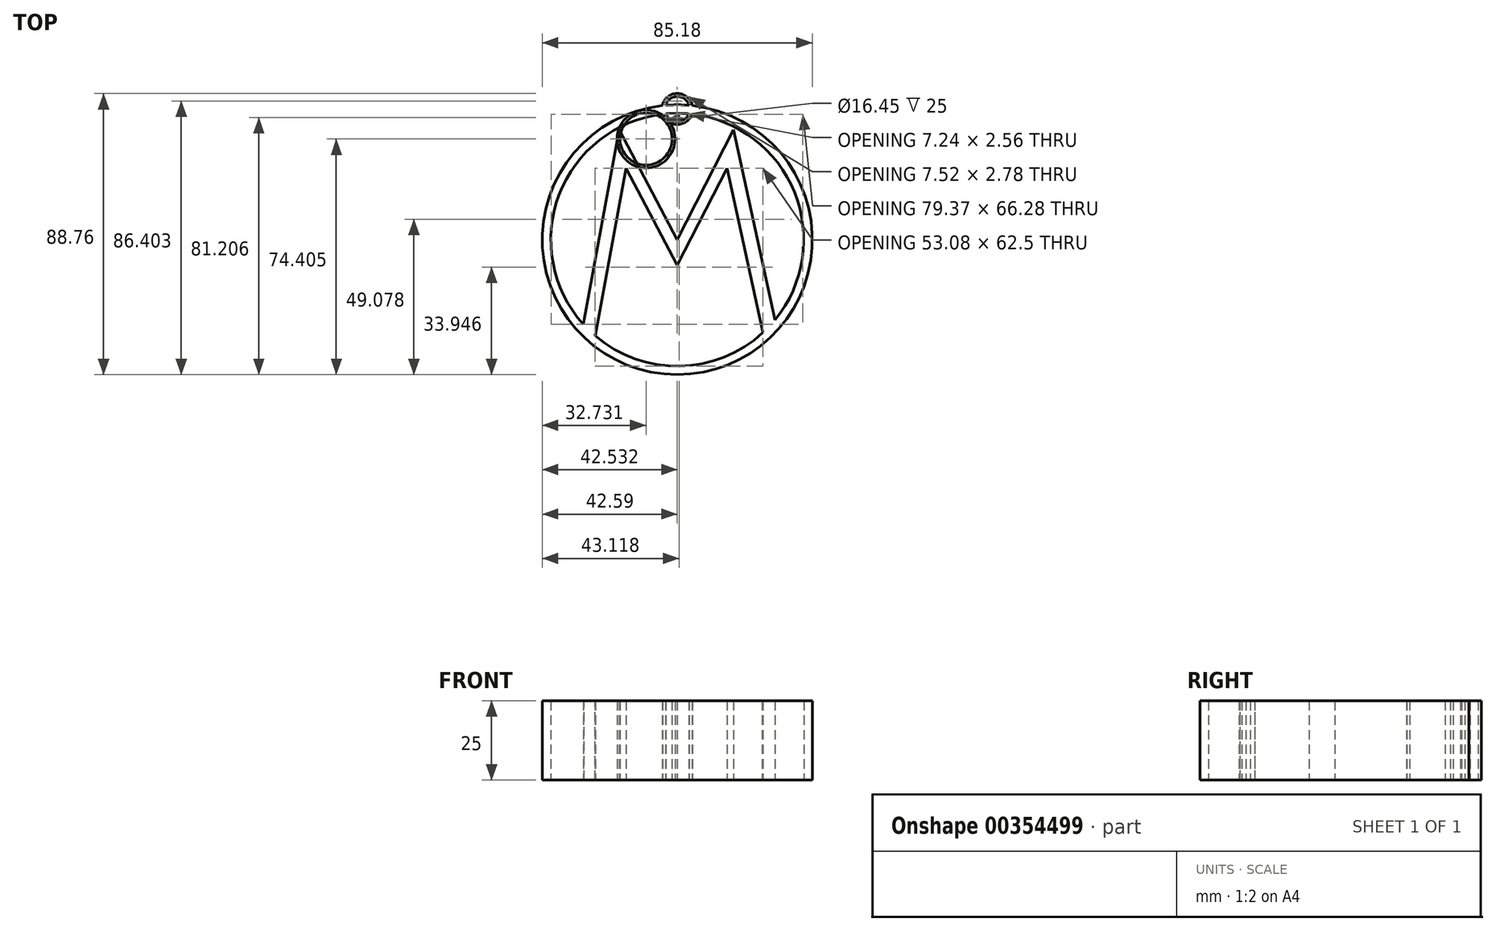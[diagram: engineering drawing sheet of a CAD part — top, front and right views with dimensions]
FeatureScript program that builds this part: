
annotation { "Feature Type Name" : "Feature", "Feature Type Description" : "" }
export const myFeature = defineFeature(function(context is Context, id is Id, definition is map)
    precondition{}
    {
        {
            var Q0;
            Q0=qCreatedBy(makeId("Top.planeOp"),FACE);
            var sketch = newSketch(context, id + "F0", { "sketchPlane" : qUnion([Q0])});
            skCircle(sketch, "E0", {"center": v(0, 0) * mm, "radius": 42.6 * mm});
            skCircle(sketch, "E1", {"center": v(0, 0) * mm, "radius": 39.9 * mm});
            skSolve(sketch);
        }
        {
            var Q0;
            Q0 = qSketchRegion(id + "F0", true);
            extrude(context, id + "F1", {"entities" : qUnion([Q0]), "depth" : 25 * mm});
        }
        {
            var Q0;
            Q0=qCreatedBy(makeId("Top.planeOp"),FACE);
            var sketch = newSketch(context, id + "F2", { "sketchPlane" : qUnion([Q0])});
            skLineSegment(sketch, "E2", {"start": v(-29.44, -25.55) * mm, "end": v(-18.38, 34.82) * mm});
            skLineSegment(sketch, "E3", {"start": v(-18.38, 34.82) * mm, "end": v(0, 0) * mm});
            skLineSegment(sketch, "E4", {"start": v(0, 0) * mm, "end": v(17.78, 34.82) * mm});
            skLineSegment(sketch, "E5", {"start": v(17.78, 34.82) * mm, "end": v(30.93, -25.55) * mm});
            skLineSegment(sketch, "E6", {"start": v(-25.85, -30.04) * mm, "end": v(-16.2, 22.6) * mm});
            skLineSegment(sketch, "E7", {"start": v(-16.2, 22.6) * mm, "end": v(0, -8.1) * mm});
            skLineSegment(sketch, "E8", {"start": v(0, -8.1) * mm, "end": v(15.68, 22.6) * mm});
            skLineSegment(sketch, "E9", {"start": v(15.68, 22.6) * mm, "end": v(26.72, -28.08) * mm});
            skLineSegment(sketch, "E10", {"start": v(-29.44, -25.55) * mm, "end": v(-25.85, -30.04) * mm});
            skLineSegment(sketch, "E11", {"start": v(26.72, -28.08) * mm, "end": v(30.93, -25.55) * mm});
            skLineSegment(sketch, "E12", {"start": v(30.93, -25.55) * mm, "end": v(26.72, -30.04) * mm});
            skLineSegment(sketch, "E13", {"start": v(26.72, -30.04) * mm, "end": v(30.93, -25.55) * mm});
            skLineSegment(sketch, "E14", {"start": v(-25.85, -30.04) * mm, "end": v(-29.44, -29.38) * mm});
            skLineSegment(sketch, "E15", {"start": v(-29.44, -25.55) * mm, "end": v(-29.44, -29.38) * mm});
            skSolve(sketch);
        }
        {
            var Q0;
            Q0=makeQuery(id+"F2.imprint","IMPRINT",FACE,{"disambiguationData":[TD([[makeQuery(id+"F2.imprint","IMPRINT",EDGE,{"derivedFrom":sQuery(id+"F2.wireOp",EDGE,"E2")}),-1.0]])]});
            extrude(context, id + "F3", {"entities" : qUnion([Q0]), "operationType" : NewBodyOperationType.ADD, "depth" : 25 * mm});
        }
        {
            var Q0;
            Q0=qCreatedBy(makeId("Top.planeOp"),FACE);
            var sketch = newSketch(context, id + "F4", { "sketchPlane" : qUnion([Q0])});
            skLineSegment(sketch, "E16", {"start": v(-29.13, -24.09) * mm, "end": v(-30.02, -28.17) * mm});
            skLineSegment(sketch, "E17", {"start": v(-30.02, -28.17) * mm, "end": v(-26.38, -32) * mm});
            skLineSegment(sketch, "E18", {"start": v(-26.38, -32) * mm, "end": v(-25.58, -28.17) * mm});
            skLineSegment(sketch, "E19", {"start": v(-25.58, -28.17) * mm, "end": v(-29.13, -24.09) * mm});
            skSolve(sketch);
        }
        {
            var Q0;
            Q0 = qSketchRegion(id + "F4", true);
            extrude(context, id + "F5", {"entities" : qUnion([Q0]), "operationType" : NewBodyOperationType.ADD, "depth" : 25 * mm});
        }
        {
            var Q0;
            Q0=qCreatedBy(makeId("Top.planeOp"),FACE);
            var sketch = newSketch(context, id + "F6", { "sketchPlane" : qUnion([Q0])});
            skLineSegment(sketch, "E20", {"start": v(26.4, -26.49) * mm, "end": v(27.47, -31.02) * mm});
            skLineSegment(sketch, "E21", {"start": v(27.47, -31.02) * mm, "end": v(30.93, -26.3) * mm});
            skLineSegment(sketch, "E22", {"start": v(30.93, -26.3) * mm, "end": v(29.96, -24.35) * mm});
            skLineSegment(sketch, "E23", {"start": v(29.96, -24.35) * mm, "end": v(26.4, -26.49) * mm});
            skSolve(sketch);
        }
        {
            var Q0;
            Q0 = qSketchRegion(id + "F6", true);
            extrude(context, id + "F7", {"entities" : qUnion([Q0]), "operationType" : NewBodyOperationType.ADD, "depth" : 25 * mm});
        }
        {
            var Q0;
            Q0=qCreatedBy(makeId("Top.planeOp"),FACE);
            var sketch = newSketch(context, id + "F8", { "sketchPlane" : qUnion([Q0])});
            skCircle(sketch, "E24", {"center": v(0, 41.27) * mm, "radius": 4.9 * mm});
            skCircle(sketch, "E25", {"center": v(0, 41.27) * mm, "radius": 3.93 * mm});
            skSolve(sketch);
        }
        {
            var Q0;
            Q0=makeQuery(id+"F8.imprint","IMPRINT",FACE,{"disambiguationData":[TD([[makeQuery(id+"F8.imprint","IMPRINT",EDGE,{"derivedFrom":sQuery(id+"F8.wireOp",EDGE,"E24")}),1.0]])]});
            extrude(context, id + "F9", {"entities" : qUnion([Q0]), "operationType" : NewBodyOperationType.ADD, "depth" : 25 * mm});
        }
        {
            var Q0;
            Q0=qCreatedBy(makeId("Top.planeOp"),FACE);
            var sketch = newSketch(context, id + "F10", { "sketchPlane" : qUnion([Q0])});
            skCircle(sketch, "E26", {"center": v(-9.86, 31.82) * mm, "radius": 9.16 * mm});
            skCircle(sketch, "E27", {"center": v(-9.86, 31.82) * mm, "radius": 8.22 * mm});
            skSolve(sketch);
        }
        {
            var Q0;
            Q0=sQuery(id+"F10.wireOp",EDGE,"E27");
            var Q1;
            Q1=sQuery(id+"F10.wireOp",EDGE,"E26");
            extrude(context, id + "F11", {"bodyType" : ToolBodyType.SURFACE, "surfaceEntities" : qUnion([Q0, Q1]), "depth" : 25 * mm});
        }
        {
            var Q0;
            Q0 = qSketchRegion(id + "F10", true);
            extrude(context, id + "F12", {"entities" : qUnion([Q0]), "depth" : 25 * mm});
        }
    });
